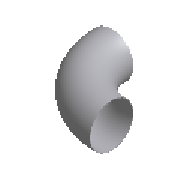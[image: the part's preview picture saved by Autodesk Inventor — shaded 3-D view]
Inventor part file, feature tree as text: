
AUTODESK INVENTOR PART (.ipt)
format: ipt  version: 2025 (Build 290162010, 162A)  size: 183,296 bytes
history: native  units: mm (DEFAULTED — no unit token found)
features: other x4, sweep x1
ambient origin geometry x8: Origin, YZ Plane, XZ Plane, XY Plane, X Axis, Y Axis, Z Axis, Center Point
bodies: Solid1 (feature_tree)
feature tree (5):
  sweep  "Sweep1"
  other  "Work Point1"
  other  "Work Axis1"
  other  "Work Point2"
  other  "Work Axis2"
